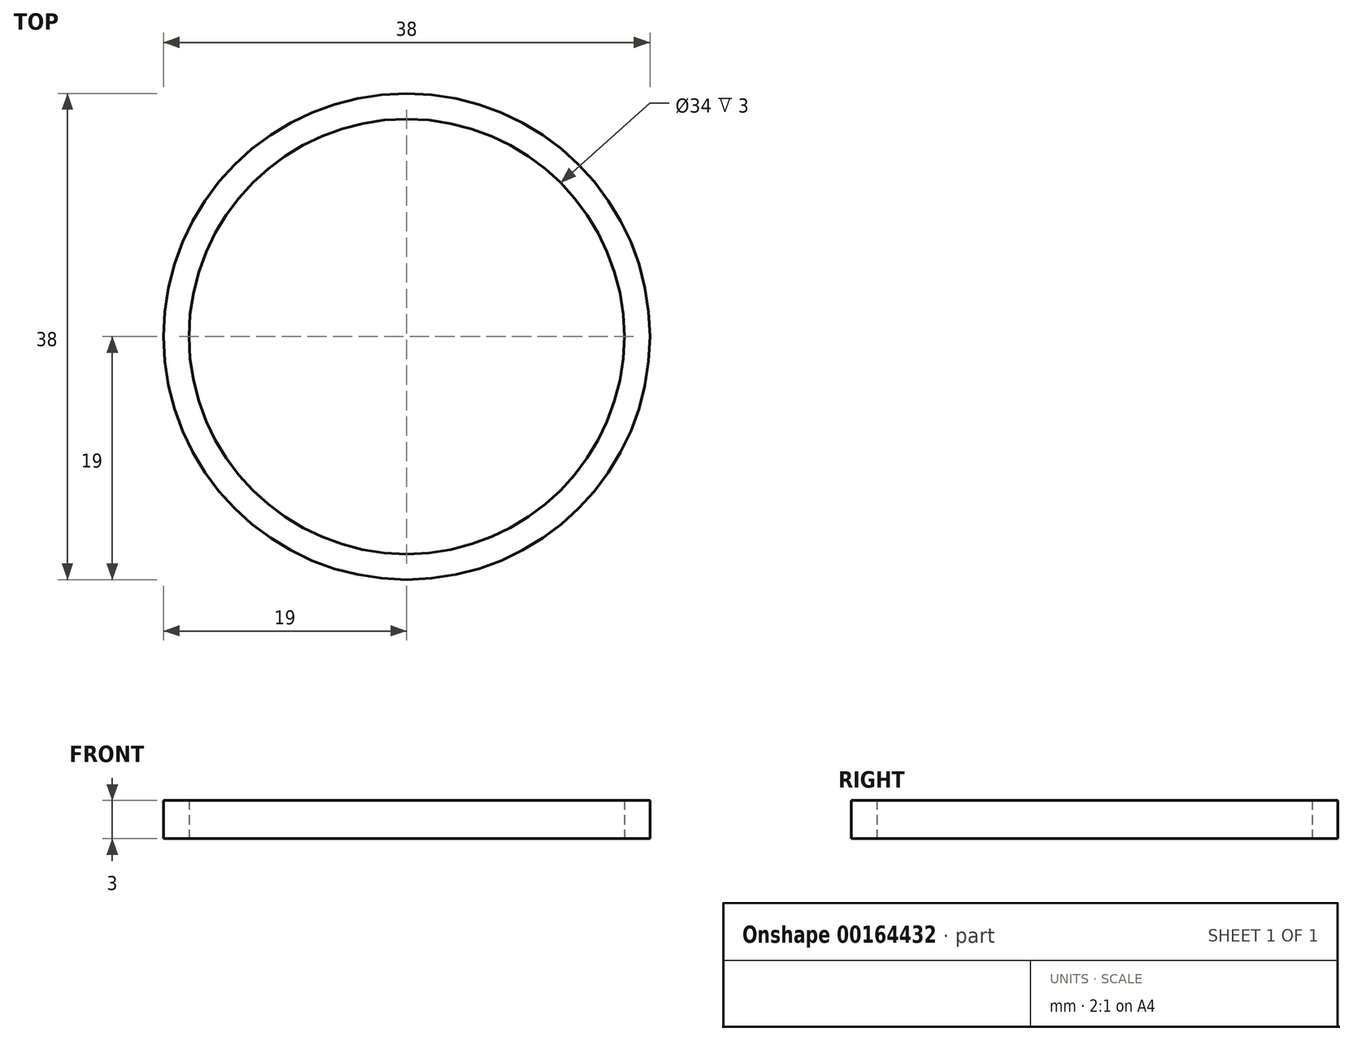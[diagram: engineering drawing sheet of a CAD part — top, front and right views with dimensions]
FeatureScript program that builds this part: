
annotation { "Feature Type Name" : "Feature", "Feature Type Description" : "" }
export const myFeature = defineFeature(function(context is Context, id is Id, definition is map)
    precondition{}
    {
        {
            var Q0;
            Q0=qCreatedBy(makeId("Top.planeOp"),FACE);
            var sketch = newSketch(context, id + "F0", { "sketchPlane" : qUnion([Q0])});
            skCircle(sketch, "E0", {"center": v(0, 0) * mm, "radius": 17 * mm});
            skCircle(sketch, "E1", {"center": v(0, 0) * mm, "radius": 19 * mm});
            skSolve(sketch);
        }
        {
            var Q0;
            Q0=makeQuery(id+"F0.imprint","IMPRINT",FACE,{"disambiguationData":[TD([[makeQuery(id+"F0.imprint","IMPRINT",EDGE,{"derivedFrom":sQuery(id+"F0.wireOp",EDGE,"E0")}),-1.0]])]});
            extrude(context, id + "F1", {"entities" : qUnion([Q0]), "depth" : 3 * mm});
        }
    });
